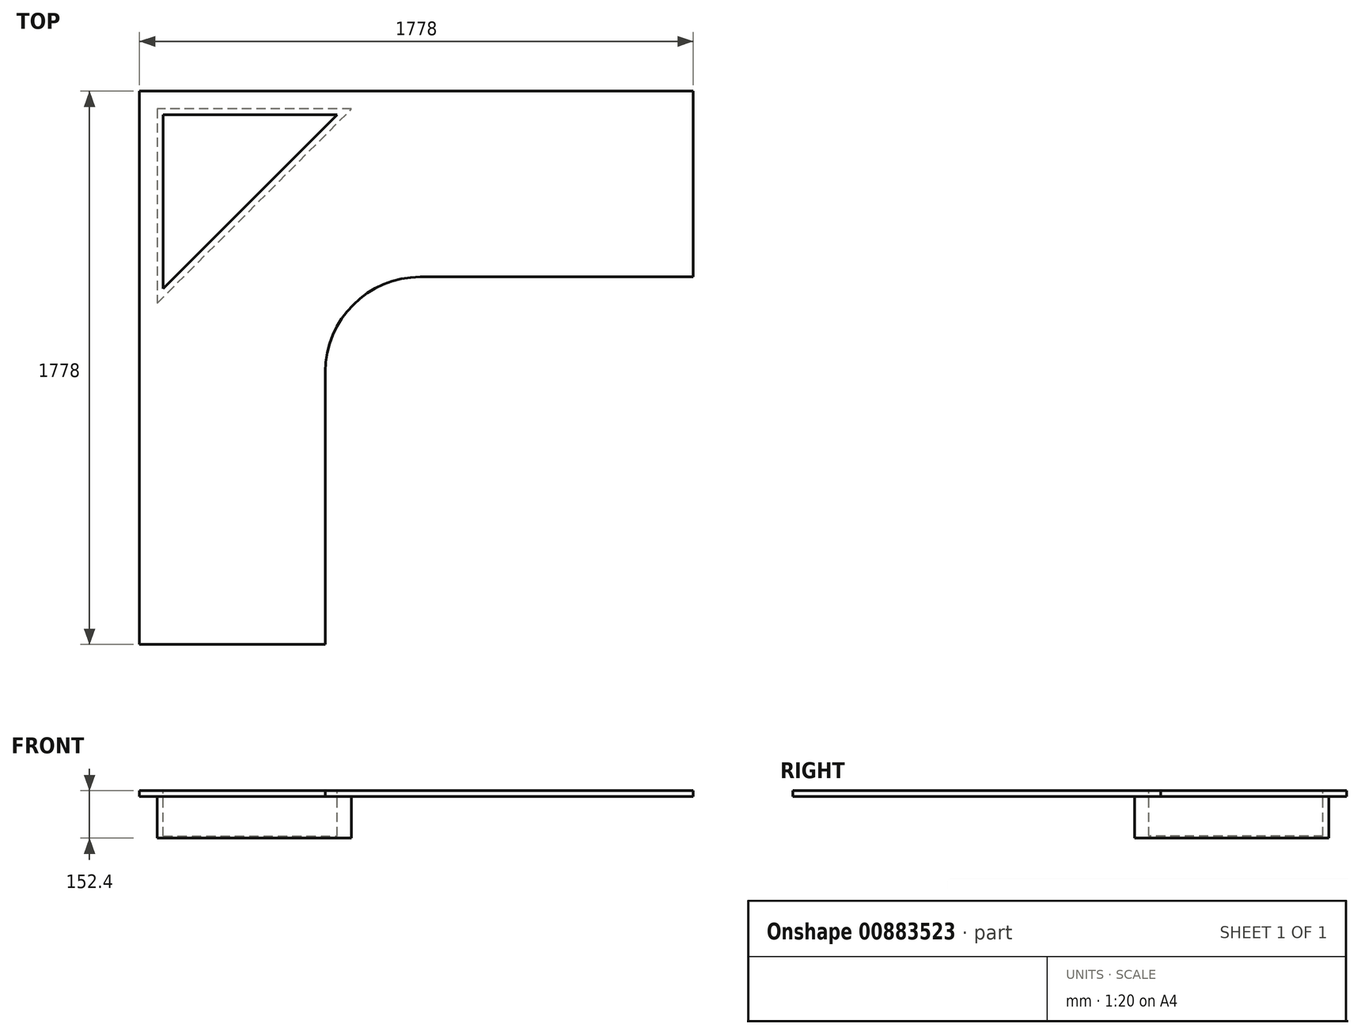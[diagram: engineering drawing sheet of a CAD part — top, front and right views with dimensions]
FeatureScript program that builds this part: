
annotation { "Feature Type Name" : "Feature", "Feature Type Description" : "" }
export const myFeature = defineFeature(function(context is Context, id is Id, definition is map)
    precondition{}
    {
        {
            var Q0;
            Q0=qCreatedBy(makeId("Top.planeOp"),FACE);
            var sketch = newSketch(context, id + "F0", { "sketchPlane" : qUnion([Q0])});
            skLineSegment(sketch, "E0.top", {"start": v(-596.9, -906.93) * mm, "end": v(0, -906.93) * mm});
            skLineSegment(sketch, "E0.left", {"start": v(-596.9, 871.07) * mm, "end": v(-596.9, -906.93) * mm});
            skLineSegment(sketch, "E1.bottom", {"start": v(-596.9, 871.07) * mm, "end": v(1181.1, 871.07) * mm});
            skLineSegment(sketch, "E1.right", {"start": v(1181.1, 871.07) * mm, "end": v(1181.1, 274.17) * mm});
            skLineSegment(sketch, "E2", {"start": v(0, -906.93) * mm, "end": v(0, -30.63) * mm});
            skLineSegment(sketch, "E3", {"start": v(1181.1, 274.17) * mm, "end": v(304.8, 274.17) * mm});
            skArc(sketch, "E4", {"start": v(304.8, 274.17) * mm, "mid": v(89.27, 184.9) * mm, "end": v(0, -30.63) * mm});
            skLineSegment(sketch, "E5", {"start": v(-520.7, 236.07) * mm, "end": v(38.1, 794.87) * mm});
            skLineSegment(sketch, "E6", {"start": v(-520.7, 794.87) * mm, "end": v(-520.7, 236.07) * mm});
            skLineSegment(sketch, "E7", {"start": v(-520.7, 794.87) * mm, "end": v(38.1, 794.87) * mm});
            skLineSegment(sketch, "E8", {"start": v(-539.75, 813.92) * mm, "end": v(-539.75, 190.08) * mm});
            skLineSegment(sketch, "E9", {"start": v(-539.75, 190.08) * mm, "end": v(84.1, 813.92) * mm});
            skLineSegment(sketch, "E10", {"start": v(84.1, 813.92) * mm, "end": v(-539.75, 813.92) * mm});
            skSolve(sketch);
        }
        {
            var Q0;
            Q0 = qSketchRegion(id + "F0", true);
            var Q1;
            Q1=makeQuery(id+"F0.imprint","IMPRINT",FACE,{"disambiguationData":[TD([[makeQuery(id+"F0.imprint","IMPRINT",EDGE,{"derivedFrom":sQuery(id+"F0.wireOp",EDGE,"E5")}),1.0]])]});
            var Q2;
            Q2=makeQuery(id+"F0.imprint","IMPRINT",FACE,{"disambiguationData":[TD([[makeQuery(id+"F0.imprint","IMPRINT",EDGE,{"derivedFrom":sQuery(id+"F0.wireOp",EDGE,"E5")}),-1.0]])]});
            extrude(context, id + "F1", {"entities" : qUnion([Q0, Q1, Q2]), "oppositeDirection" : true, "depth" : 19.05 * mm, "offsetDistance" : 25.4 * mm});
        }
        {
            var Q0;
            Q0=makeQuery(id+"F0.imprint","IMPRINT",FACE,{"disambiguationData":[TD([[makeQuery(id+"F0.imprint","IMPRINT",EDGE,{"derivedFrom":sQuery(id+"F0.wireOp",EDGE,"E5")}),-1.0]])]});
            extrude(context, id + "F2", {"entities" : qUnion([Q0]), "operationType" : NewBodyOperationType.ADD, "oppositeDirection" : true, "depth" : 152.4 * mm, "offsetDistance" : 25.4 * mm});
        }
        {
            var Q0;
            Q0=makeQuery(id+"F0.imprint","IMPRINT",FACE,{"disambiguationData":[TD([[makeQuery(id+"F0.imprint","IMPRINT",EDGE,{"derivedFrom":sQuery(id+"F0.wireOp",EDGE,"E5")}),1.0]])]});
            extrude(context, id + "F3", {"entities" : qUnion([Q0]), "operationType" : NewBodyOperationType.ADD, "oppositeDirection" : true, "depth" : 152.4 * mm, "offsetDistance" : 25.4 * mm});
        }
        {
            var Q0;
            Q0=makeQuery(id+"F0.imprint","IMPRINT",FACE,{"disambiguationData":[TD([[makeQuery(id+"F0.imprint","IMPRINT",EDGE,{"derivedFrom":sQuery(id+"F0.wireOp",EDGE,"E5")}),1.0]])]});
            extrude(context, id + "F4", {"entities" : qUnion([Q0]), "operationType" : NewBodyOperationType.REMOVE, "oppositeDirection" : true, "depth" : 146.05 * mm, "offsetDistance" : 25.4 * mm});
        }
    });
